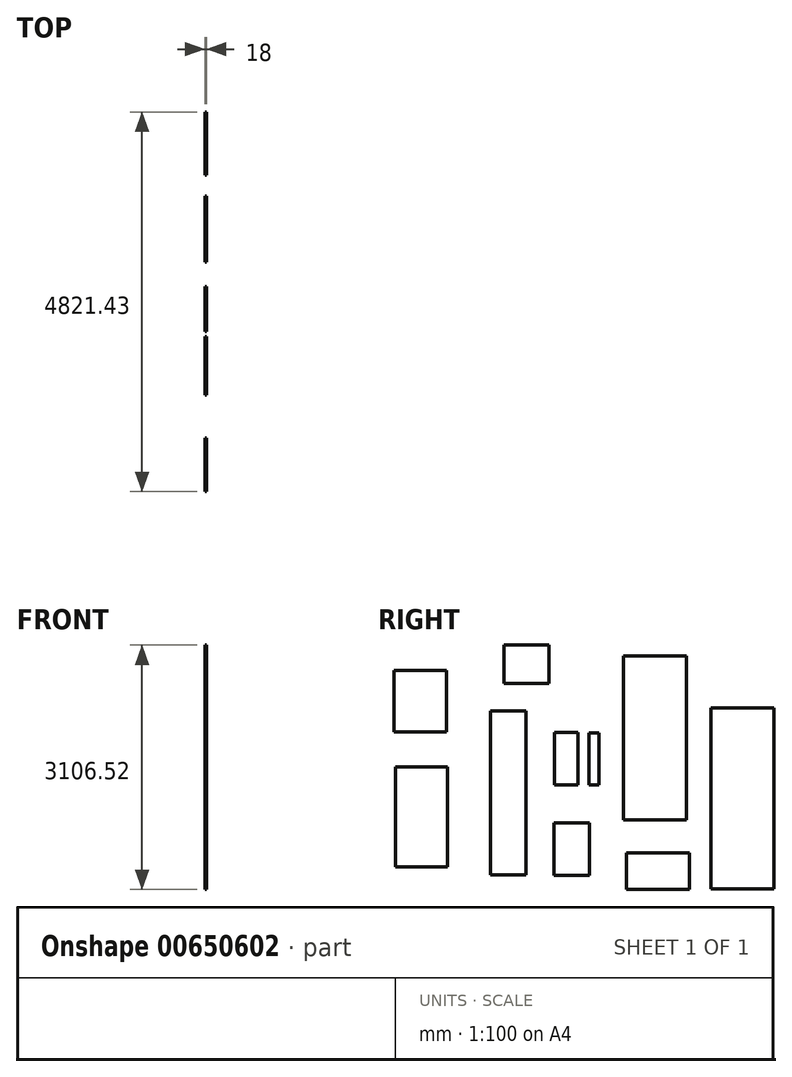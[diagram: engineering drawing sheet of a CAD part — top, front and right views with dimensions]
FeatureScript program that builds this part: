
annotation { "Feature Type Name" : "Feature", "Feature Type Description" : "" }
export const myFeature = defineFeature(function(context is Context, id is Id, definition is map)
    precondition{}
    {
        {
            var Q0;
            Q0=qCreatedBy(makeId("Right.planeOp"),FACE);
            var sketch = newSketch(context, id + "F0", { "sketchPlane" : qUnion([Q0])});
            skLineSegment(sketch, "E0.bottom", {"start": v(-38.9, 1994.37) * mm, "end": v(761.1, 1994.37) * mm});
            skLineSegment(sketch, "E0.top", {"start": v(-38.9, -85.63) * mm, "end": v(761.1, -85.63) * mm});
            skLineSegment(sketch, "E0.left", {"start": v(-38.9, 1994.37) * mm, "end": v(-38.9, -85.63) * mm});
            skLineSegment(sketch, "E0.right", {"start": v(761.1, 1994.37) * mm, "end": v(761.1, -85.63) * mm});
            skLineSegment(sketch, "E1.bottom", {"start": v(-1727.59, 1295.14) * mm, "end": v(-1277.59, 1295.14) * mm});
            skLineSegment(sketch, "E1.top", {"start": v(-1727.59, -784.86) * mm, "end": v(-1277.59, -784.86) * mm});
            skLineSegment(sketch, "E1.left", {"start": v(-1727.59, 1295.14) * mm, "end": v(-1727.59, -784.86) * mm});
            skLineSegment(sketch, "E1.right", {"start": v(-1277.59, 1295.14) * mm, "end": v(-1277.59, -784.86) * mm});
            skLineSegment(sketch, "E2.bottom", {"start": v(-921.94, -125.65) * mm, "end": v(-471.94, -125.65) * mm});
            skLineSegment(sketch, "E2.top", {"start": v(-921.94, -789.65) * mm, "end": v(-471.94, -789.65) * mm});
            skLineSegment(sketch, "E2.left", {"start": v(-921.94, -125.65) * mm, "end": v(-921.94, -789.65) * mm});
            skLineSegment(sketch, "E2.right", {"start": v(-471.94, -125.65) * mm, "end": v(-471.94, -789.65) * mm});
            skLineSegment(sketch, "E3.bottom", {"start": v(1068.15, 1333.6) * mm, "end": v(1868.15, 1333.6) * mm});
            skLineSegment(sketch, "E3.top", {"start": v(1068.15, -966.4) * mm, "end": v(1868.15, -966.4) * mm});
            skLineSegment(sketch, "E3.left", {"start": v(1068.15, 1333.6) * mm, "end": v(1068.15, -966.4) * mm});
            skLineSegment(sketch, "E3.right", {"start": v(1868.15, 1333.6) * mm, "end": v(1868.15, -966.4) * mm});
            skLineSegment(sketch, "E4.bottom", {"start": v(-2937, 585.04) * mm, "end": v(-2273, 585.04) * mm});
            skLineSegment(sketch, "E4.top", {"start": v(-2937, -682.96) * mm, "end": v(-2273, -682.96) * mm});
            skLineSegment(sketch, "E4.left", {"start": v(-2937, 585.04) * mm, "end": v(-2937, -682.96) * mm});
            skLineSegment(sketch, "E4.right", {"start": v(-2273, 585.04) * mm, "end": v(-2273, -682.96) * mm});
            skLineSegment(sketch, "E5.bottom", {"start": v(0, -508.87) * mm, "end": v(800, -508.87) * mm});
            skLineSegment(sketch, "E5.top", {"start": v(0, -972.87) * mm, "end": v(800, -972.87) * mm});
            skLineSegment(sketch, "E5.left", {"start": v(0, -508.87) * mm, "end": v(0, -972.87) * mm});
            skLineSegment(sketch, "E5.right", {"start": v(800, -508.87) * mm, "end": v(800, -972.87) * mm});
            skLineSegment(sketch, "E6.bottom", {"start": v(-2953.28, 1813) * mm, "end": v(-2289.28, 1813) * mm});
            skLineSegment(sketch, "E6.top", {"start": v(-2953.28, 1031) * mm, "end": v(-2289.28, 1031) * mm});
            skLineSegment(sketch, "E6.left", {"start": v(-2953.28, 1813) * mm, "end": v(-2953.28, 1031) * mm});
            skLineSegment(sketch, "E6.right", {"start": v(-2289.28, 1813) * mm, "end": v(-2289.28, 1031) * mm});
            skLineSegment(sketch, "E7.bottom", {"start": v(-917.7, 1021.72) * mm, "end": v(-615.7, 1021.72) * mm});
            skLineSegment(sketch, "E7.top", {"start": v(-917.7, 357.72) * mm, "end": v(-615.7, 357.72) * mm});
            skLineSegment(sketch, "E7.left", {"start": v(-917.7, 1021.72) * mm, "end": v(-917.7, 357.72) * mm});
            skLineSegment(sketch, "E7.right", {"start": v(-615.7, 1021.72) * mm, "end": v(-615.7, 357.72) * mm});
            skLineSegment(sketch, "E8.bottom", {"start": v(-479.57, 1018.13) * mm, "end": v(-349.57, 1018.13) * mm});
            skLineSegment(sketch, "E8.top", {"start": v(-479.57, 354.13) * mm, "end": v(-349.57, 354.13) * mm});
            skLineSegment(sketch, "E8.left", {"start": v(-479.57, 1018.13) * mm, "end": v(-479.57, 354.13) * mm});
            skLineSegment(sketch, "E8.right", {"start": v(-349.57, 1018.13) * mm, "end": v(-349.57, 354.13) * mm});
            skLineSegment(sketch, "E9.bottom", {"start": v(-1561.66, 2133.65) * mm, "end": v(-986.66, 2133.65) * mm});
            skLineSegment(sketch, "E9.top", {"start": v(-1561.66, 1643.65) * mm, "end": v(-986.66, 1643.65) * mm});
            skLineSegment(sketch, "E9.left", {"start": v(-1561.66, 2133.65) * mm, "end": v(-1561.66, 1643.65) * mm});
            skLineSegment(sketch, "E9.right", {"start": v(-986.66, 2133.65) * mm, "end": v(-986.66, 1643.65) * mm});
            skSolve(sketch);
        }
        {
            var Q0;
            Q0=makeQuery(id+"F0.imprint","IMPRINT",FACE,{"disambiguationData":[TD([[makeQuery(id+"F0.imprint","IMPRINT",EDGE,{"derivedFrom":sQuery(id+"F0.wireOp",EDGE,"E1.bottom")}),-1.0]])]});
            var Q1;
            Q1=makeQuery(id+"F0.imprint","IMPRINT",FACE,{"disambiguationData":[TD([[makeQuery(id+"F0.imprint","IMPRINT",EDGE,{"derivedFrom":sQuery(id+"F0.wireOp",EDGE,"eLXkUhCD-NmAt-3djJ-aWTH-lgNmqVTxMkS5.bottom")}),-1.0]])]});
            var Q2;
            Q2=makeQuery(id+"F0.imprint","IMPRINT",FACE,{"disambiguationData":[TD([[makeQuery(id+"F0.imprint","IMPRINT",EDGE,{"derivedFrom":sQuery(id+"F0.wireOp",EDGE,"E2.bottom")}),-1.0]])]});
            var Q3;
            Q3=makeQuery(id+"F0.imprint","IMPRINT",FACE,{"disambiguationData":[TD([[makeQuery(id+"F0.imprint","IMPRINT",EDGE,{"derivedFrom":sQuery(id+"F0.wireOp",EDGE,"E0.bottom")}),-1.0]])]});
            var Q4;
            Q4=makeQuery(id+"F0.imprint","IMPRINT",FACE,{"disambiguationData":[TD([[makeQuery(id+"F0.imprint","IMPRINT",EDGE,{"derivedFrom":sQuery(id+"F0.wireOp",EDGE,"E3.bottom")}),-1.0]])]});
            var Q5;
            Q5=makeQuery(id+"F0.imprint","IMPRINT",FACE,{"disambiguationData":[TD([[makeQuery(id+"F0.imprint","IMPRINT",EDGE,{"derivedFrom":sQuery(id+"F0.wireOp",EDGE,"E4.bottom")}),-1.0]])]});
            var Q6;
            Q6=makeQuery(id+"F0.imprint","IMPRINT",FACE,{"disambiguationData":[TD([[makeQuery(id+"F0.imprint","IMPRINT",EDGE,{"derivedFrom":sQuery(id+"F0.wireOp",EDGE,"E5.bottom")}),-1.0]])]});
            var Q7;
            Q7=makeQuery(id+"F0.imprint","IMPRINT",FACE,{"disambiguationData":[TD([[makeQuery(id+"F0.imprint","IMPRINT",EDGE,{"derivedFrom":sQuery(id+"F0.wireOp",EDGE,"E6.bottom")}),-1.0]])]});
            var Q8;
            Q8=makeQuery(id+"F0.imprint","IMPRINT",FACE,{"disambiguationData":[TD([[makeQuery(id+"F0.imprint","IMPRINT",EDGE,{"derivedFrom":sQuery(id+"F0.wireOp",EDGE,"E7.bottom")}),-1.0]])]});
            var Q9;
            Q9=makeQuery(id+"F0.imprint","IMPRINT",FACE,{"disambiguationData":[TD([[makeQuery(id+"F0.imprint","IMPRINT",EDGE,{"derivedFrom":sQuery(id+"F0.wireOp",EDGE,"E8.bottom")}),-1.0]])]});
            var Q10;
            Q10=makeQuery(id+"F0.imprint","IMPRINT",FACE,{"disambiguationData":[TD([[makeQuery(id+"F0.imprint","IMPRINT",EDGE,{"derivedFrom":sQuery(id+"F0.wireOp",EDGE,"E9.bottom")}),-1.0]])]});
            extrude(context, id + "F1", {"entities" : qUnion([Q0, Q1, Q2, Q3, Q4, Q5, Q6, Q7, Q8, Q9, Q10]), "depth" : 18 * mm, "offsetDistance" : 25 * mm});
        }
    });
